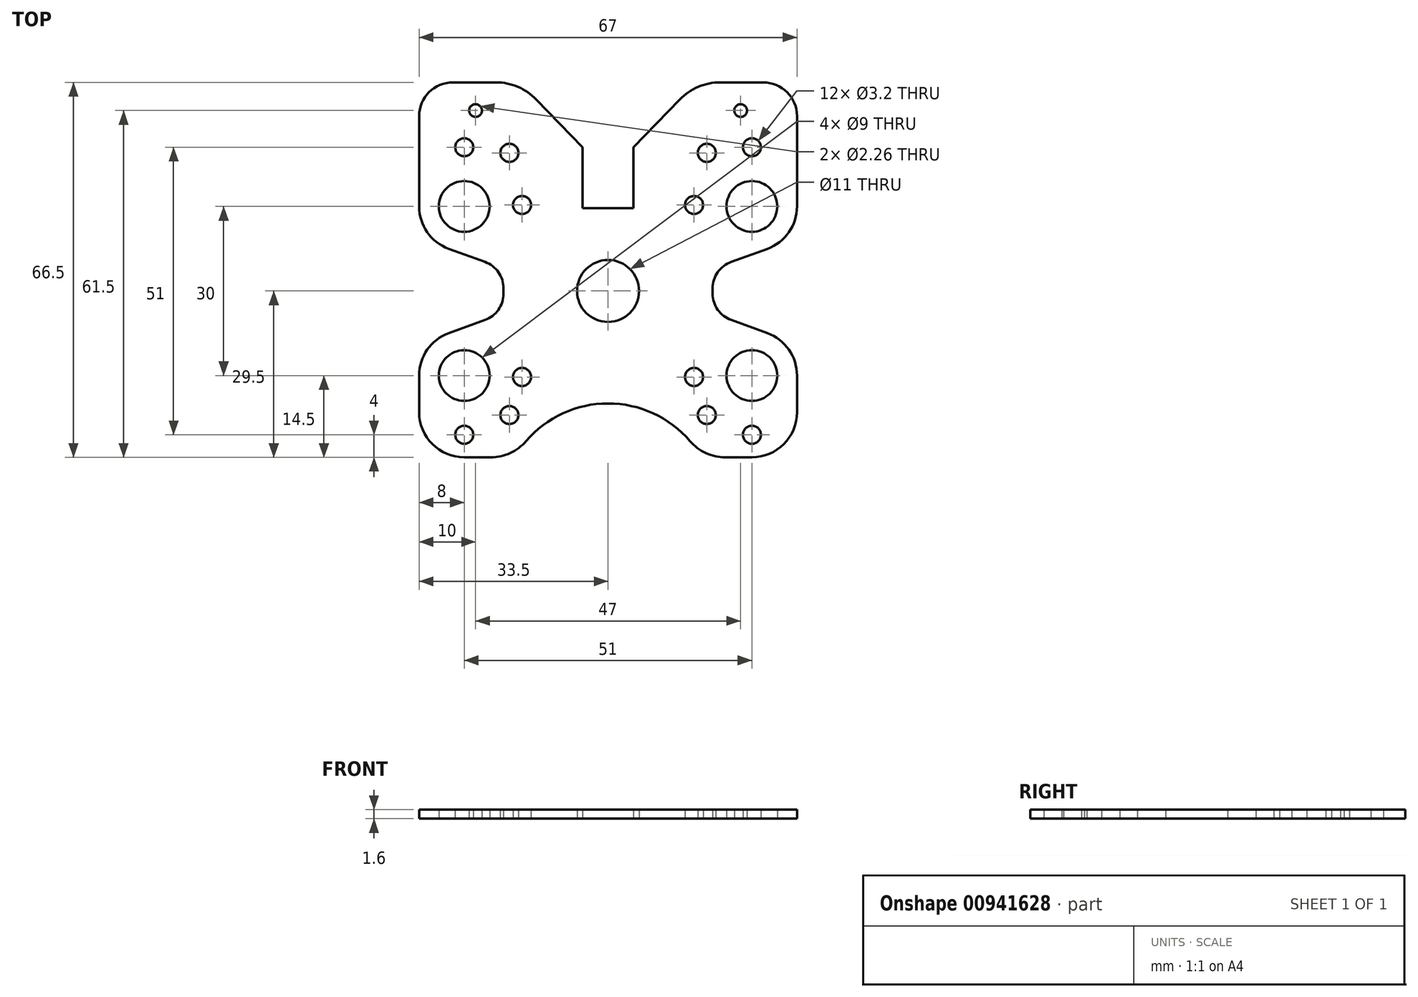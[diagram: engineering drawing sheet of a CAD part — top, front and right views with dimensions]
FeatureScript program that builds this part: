
annotation { "Feature Type Name" : "Feature", "Feature Type Description" : "" }
export const myFeature = defineFeature(function(context is Context, id is Id, definition is map)
    precondition{}
    {
        {
            var Q0;
            Q0=qCreatedBy(makeId("Top.planeOp"),FACE);
            var sketch = newSketch(context, id + "F0", { "sketchPlane" : qUnion([Q0])});
            skLineSegment(sketch, "E0.bottom", {"start": v(15.25, 7.25) * mm, "end": v(-15.25, 7.25) * mm, "construction": true});
            skLineSegment(sketch, "E0.top", {"start": v(15.25, -23.25) * mm, "end": v(-15.25, -23.25) * mm, "construction": true});
            skLineSegment(sketch, "E0.left", {"start": v(15.25, 7.25) * mm, "end": v(15.25, -23.25) * mm, "construction": true});
            skLineSegment(sketch, "E0.right", {"start": v(-15.25, 7.25) * mm, "end": v(-15.25, -23.25) * mm, "construction": true});
            skPoint(sketch, "E0.middle", {"position": v(0, -8) * mm});
            skLineSegment(sketch, "E1.bottom", {"start": v(25.5, 17.5) * mm, "end": v(-25.5, 17.5) * mm, "construction": true});
            skLineSegment(sketch, "E1.top", {"start": v(25.5, -33.5) * mm, "end": v(-25.5, -33.5) * mm, "construction": true});
            skLineSegment(sketch, "E1.left", {"start": v(25.5, 17.5) * mm, "end": v(25.5, -33.5) * mm, "construction": true});
            skLineSegment(sketch, "E1.right", {"start": v(-25.5, 17.5) * mm, "end": v(-25.5, -33.5) * mm, "construction": true});
            skCircle(sketch, "E2", {"center": v(-25.5, 17.5) * mm, "radius": 1.6 * mm});
            skCircle(sketch, "E3", {"center": v(25.5, 17.5) * mm, "radius": 1.6 * mm});
            skCircle(sketch, "E4", {"center": v(-25.5, -33.5) * mm, "radius": 1.6 * mm});
            skCircle(sketch, "E5", {"center": v(25.5, -33.5) * mm, "radius": 1.6 * mm});
            skCircle(sketch, "E6", {"center": v(-15.25, -23.25) * mm, "radius": 1.6 * mm});
            skCircle(sketch, "E7", {"center": v(15.25, -23.25) * mm, "radius": 1.6 * mm});
            skCircle(sketch, "E8", {"center": v(-15.25, 7.25) * mm, "radius": 1.6 * mm});
            skCircle(sketch, "E9", {"center": v(15.25, 7.25) * mm, "radius": 1.6 * mm});
            skLineSegment(sketch, "E10", {"start": v(-4.5, 6.68) * mm, "end": v(-4.5, 17.5) * mm});
            skLineSegment(sketch, "E11", {"start": v(-4.5, 17.5) * mm, "end": v(-10.72, 23.9) * mm});
            skLineSegment(sketch, "E12", {"start": v(-4.5, 6.68) * mm, "end": v(0, 6.68) * mm});
            skCircle(sketch, "E13", {"center": v(-23.5, 24) * mm, "radius": 1.13 * mm});
            skPoint(sketch, "E13.first.point", {"position": v(-24.6, 24.3) * mm});
            skPoint(sketch, "E13.second.point", {"position": v(-22.4, 24.3) * mm});
            skPoint(sketch, "E13.third.point", {"position": v(-23.5, 22.87) * mm});
            skCircle(sketch, "E14", {"center": v(-17.5, 16.5) * mm, "radius": 1.13 * mm, "construction": true});
            skPoint(sketch, "E14.first.point", {"position": v(-18.63, 16.5) * mm});
            skPoint(sketch, "E14.second.point", {"position": v(-17.2, 17.6) * mm});
            skPoint(sketch, "E14.third.point", {"position": v(-16.52, 15.93) * mm});
            skCircle(sketch, "E15", {"center": v(-17.5, -30) * mm, "radius": 1.13 * mm, "construction": true});
            skPoint(sketch, "E15.first.point", {"position": v(-18.63, -30) * mm});
            skPoint(sketch, "E15.second.point", {"position": v(-16.7, -30.8) * mm});
            skPoint(sketch, "E15.third.point", {"position": v(-16.93, -29.02) * mm});
            skLineSegment(sketch, "E16.bottom", {"start": v(-25.5, 7) * mm, "end": v(25.5, 7) * mm, "construction": true});
            skLineSegment(sketch, "E16.top", {"start": v(-25.5, -23) * mm, "end": v(25.5, -23) * mm, "construction": true});
            skLineSegment(sketch, "E16.left", {"start": v(-25.5, 7) * mm, "end": v(-25.5, -23) * mm, "construction": true});
            skLineSegment(sketch, "E16.right", {"start": v(25.5, 7) * mm, "end": v(25.5, -23) * mm, "construction": true});
            skCircle(sketch, "E17", {"center": v(-25.5, 7) * mm, "radius": 4.5 * mm});
            skCircle(sketch, "E18", {"center": v(-25.5, -23) * mm, "radius": 4.5 * mm});
            skCircle(sketch, "E19.MirrorC", {"center": v(25.5, 7) * mm, "radius": 4.5 * mm});
            skCircle(sketch, "E20.MirrorC", {"center": v(25.5, -23) * mm, "radius": 4.5 * mm});
            skCircle(sketch, "E21.MirrorC", {"center": v(17.5, -30) * mm, "radius": 1.13 * mm, "construction": true});
            skCircle(sketch, "E22.MirrorC", {"center": v(17.5, 16.5) * mm, "radius": 1.13 * mm, "construction": true});
            skCircle(sketch, "E23.MirrorC", {"center": v(23.5, 24) * mm, "radius": 1.13 * mm});
            skLineSegment(sketch, "E24", {"start": v(-25.5, 0) * mm, "end": v(-25.5, -16) * mm, "construction": true});
            skLineSegment(sketch, "E25", {"start": v(0, -8) * mm, "end": v(-33.11, -8) * mm, "construction": true});
            skCircle(sketch, "E26", {"center": v(0, -8) * mm, "radius": 5.5 * mm});
            skPoint(sketch, "E27", {"position": v(0, -23.25) * mm});
            skLineSegment(sketch, "E28", {"start": v(-25.5, 7) * mm, "end": v(-28.23, 14.5) * mm, "construction": true});
            skLineSegment(sketch, "E29", {"start": v(-10.72, 23.9) * mm, "end": v(-12.71, 25.96) * mm});
            skLineSegment(sketch, "E30", {"start": v(-19.89, 29) * mm, "end": v(-27.5, 29) * mm});
            skLineSegment(sketch, "E31", {"start": v(-33.5, 23) * mm, "end": v(-33.5, 7) * mm});
            skPoint(sketch, "E32.visualSharp", {"position": v(-33.5, 29) * mm});
            skArc(sketch, "E32.filletArc", {"start": v(-27.5, 29) * mm, "mid": v(-31.74, 27.24) * mm, "end": v(-33.5, 23) * mm});
            skPoint(sketch, "E33.visualSharp", {"position": v(-15.66, 29) * mm});
            skArc(sketch, "E33.filletArc", {"start": v(-12.71, 25.96) * mm, "mid": v(-16, 28.2) * mm, "end": v(-19.89, 29) * mm});
            skArc(sketch, "E34", {"start": v(-33.5, 7) * mm, "mid": v(-32.05, 2.41) * mm, "end": v(-28.24, -0.52) * mm});
            skLineSegment(sketch, "E35", {"start": v(-28.24, -0.52) * mm, "end": v(-21.82, -2.85) * mm});
            skLineSegment(sketch, "E36", {"start": v(-18.53, -7.55) * mm, "end": v(-18.53, -8) * mm});
            skLineSegment(sketch, "E37", {"start": v(-25.5, 7) * mm, "end": v(-28.24, -0.52) * mm, "construction": true});
            skPoint(sketch, "E38.visualSharp", {"position": v(-18.53, -4.05) * mm});
            skArc(sketch, "E38.filletArc", {"start": v(-18.53, -7.55) * mm, "mid": v(-19.44, -4.68) * mm, "end": v(-21.82, -2.85) * mm});
            skLineSegment(sketch, "E39.MirrorCS", {"start": v(-28.24, -15.48) * mm, "end": v(-21.82, -13.15) * mm});
            skLineSegment(sketch, "E40.MirrorCS", {"start": v(-18.53, -8.45) * mm, "end": v(-18.53, -8) * mm});
            skArc(sketch, "E41.MirrorCS", {"start": v(-18.53, -8.45) * mm, "mid": v(-19.44, -11.32) * mm, "end": v(-21.82, -13.15) * mm});
            skArc(sketch, "E42.MirrorCS", {"start": v(-33.5, -23) * mm, "mid": v(-32.05, -18.41) * mm, "end": v(-28.24, -15.48) * mm});
            skLineSegment(sketch, "E43", {"start": v(-33.5, -23) * mm, "end": v(-33.5, -29.5) * mm});
            skArc(sketch, "E44", {"start": v(-33.5, -29.5) * mm, "mid": v(-31.16, -35.16) * mm, "end": v(-25.5, -37.5) * mm});
            skLineSegment(sketch, "E45", {"start": v(-25.5, -37.5) * mm, "end": v(-20.78, -37.5) * mm});
            skArc(sketch, "E46", {"start": v(-20.78, -37.5) * mm, "mid": v(-17.34, -36.75) * mm, "end": v(-14.53, -34.63) * mm});
            skArc(sketch, "E47", {"start": v(-14.53, -34.63) * mm, "mid": v(-8, -29.7) * mm, "end": v(0, -27.95) * mm});
            skLineSegment(sketch, "E48", {"start": v(0, -27.95) * mm, "end": v(6.9, -27.95) * mm, "construction": true});
            skLineSegment(sketch, "E49.MirrorCS", {"start": v(4.5, 6.68) * mm, "end": v(0, 6.68) * mm});
            skLineSegment(sketch, "E50.MirrorCS", {"start": v(4.5, 6.68) * mm, "end": v(4.5, 17.5) * mm});
            skLineSegment(sketch, "E51.MirrorCS", {"start": v(4.5, 17.5) * mm, "end": v(10.72, 23.9) * mm});
            skLineSegment(sketch, "E52.MirrorCS", {"start": v(10.72, 23.9) * mm, "end": v(12.71, 25.96) * mm});
            skArc(sketch, "E53.MirrorCS", {"start": v(12.71, 25.96) * mm, "mid": v(16, 28.2) * mm, "end": v(19.89, 29) * mm});
            skLineSegment(sketch, "E54.MirrorCS", {"start": v(19.89, 29) * mm, "end": v(27.5, 29) * mm});
            skArc(sketch, "E55.MirrorCS", {"start": v(27.5, 29) * mm, "mid": v(31.74, 27.24) * mm, "end": v(33.5, 23) * mm});
            skLineSegment(sketch, "E56.MirrorCS", {"start": v(33.5, 23) * mm, "end": v(33.5, 7) * mm});
            skArc(sketch, "E57.MirrorCS", {"start": v(33.5, 7) * mm, "mid": v(32.05, 2.41) * mm, "end": v(28.24, -0.52) * mm});
            skLineSegment(sketch, "E58.MirrorCS", {"start": v(28.24, -0.52) * mm, "end": v(21.82, -2.85) * mm});
            skLineSegment(sketch, "E59.MirrorCS", {"start": v(18.53, -7.55) * mm, "end": v(18.53, -8) * mm});
            skLineSegment(sketch, "E60.MirrorCS", {"start": v(18.53, -8.45) * mm, "end": v(18.53, -8) * mm});
            skArc(sketch, "E61.MirrorCS", {"start": v(18.53, -7.55) * mm, "mid": v(19.44, -4.68) * mm, "end": v(21.82, -2.85) * mm});
            skArc(sketch, "E62.MirrorCS", {"start": v(18.53, -8.45) * mm, "mid": v(19.44, -11.32) * mm, "end": v(21.82, -13.15) * mm});
            skArc(sketch, "E63.MirrorCS", {"start": v(33.5, -23) * mm, "mid": v(32.05, -18.41) * mm, "end": v(28.24, -15.48) * mm});
            skLineSegment(sketch, "E64.MirrorCS", {"start": v(25.5, -37.5) * mm, "end": v(20.78, -37.5) * mm});
            skLineSegment(sketch, "E65.MirrorCS", {"start": v(33.5, -23) * mm, "end": v(33.5, -29.5) * mm});
            skArc(sketch, "E66.MirrorCS", {"start": v(33.5, -29.5) * mm, "mid": v(31.16, -35.16) * mm, "end": v(25.5, -37.5) * mm});
            skArc(sketch, "E67.MirrorCS", {"start": v(20.78, -37.5) * mm, "mid": v(17.34, -36.75) * mm, "end": v(14.53, -34.63) * mm});
            skArc(sketch, "E68.MirrorCS", {"start": v(14.53, -34.63) * mm, "mid": v(8, -29.7) * mm, "end": v(0, -27.95) * mm});
            skLineSegment(sketch, "E69", {"start": v(21.82, -13.15) * mm, "end": v(28.24, -15.48) * mm});
            skCircle(sketch, "E70", {"center": v(-25.5, 7) * mm, "radius": 7 * mm, "construction": true});
            skCircle(sketch, "E71", {"center": v(-17.5, 16.5) * mm, "radius": 1.6 * mm});
            skCircle(sketch, "E72", {"center": v(-17.5, -30) * mm, "radius": 1.6 * mm});
            skCircle(sketch, "E73.MirrorC", {"center": v(17.5, 16.5) * mm, "radius": 1.6 * mm});
            skCircle(sketch, "E74.MirrorC", {"center": v(17.5, -30) * mm, "radius": 1.6 * mm});
            skSolve(sketch);
        }
        {
            var Q0;
            Q0=makeQuery(id+"F0.imprint","IMPRINT",FACE,{"disambiguationData":[TD([[makeQuery(id+"F0.imprint","IMPRINT",EDGE,{"derivedFrom":sQuery(id+"F0.wireOp",EDGE,"E2")}),-1.0]])]});
            extrude(context, id + "F1", {"entities" : qUnion([Q0]), "depth" : 1.6 * mm, "offsetDistance" : 25 * mm});
        }
    });
